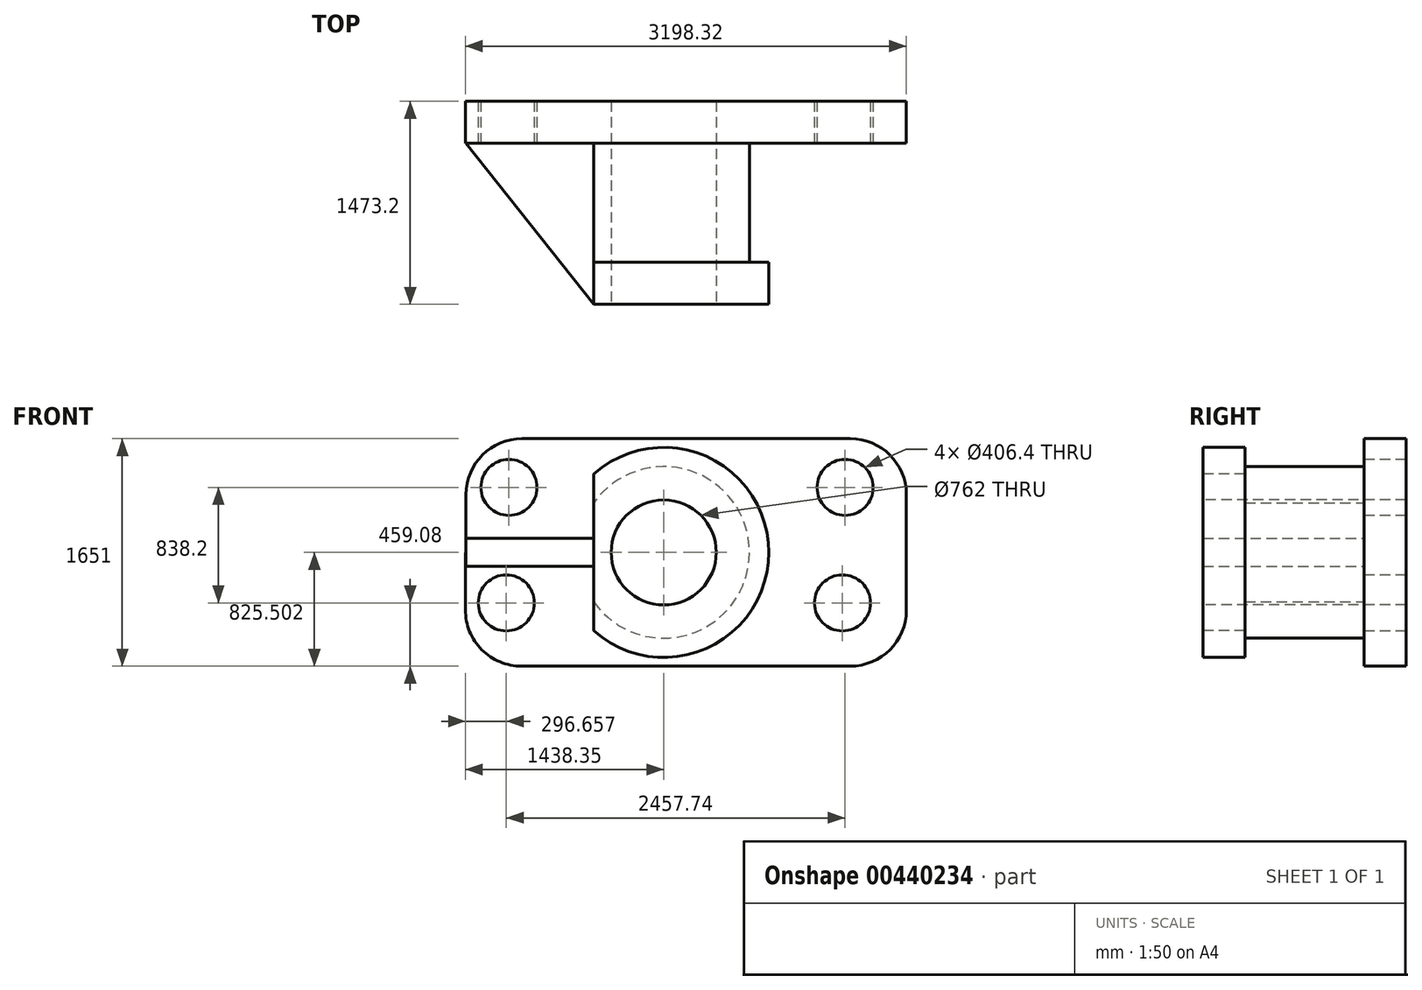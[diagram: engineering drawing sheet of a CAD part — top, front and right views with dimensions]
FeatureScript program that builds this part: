
annotation { "Feature Type Name" : "Feature", "Feature Type Description" : "" }
export const myFeature = defineFeature(function(context is Context, id is Id, definition is map)
    precondition{}
    {
        {
            var Q0;
            Q0=qCreatedBy(makeId("Front.planeOp"),FACE);
            var sketch = newSketch(context, id + "F0", { "sketchPlane" : qUnion([Q0])});
            skLineSegment(sketch, "E0", {"start": v(-1594.17, 978.7) * mm, "end": v(1597.8, 978.7) * mm});
            skLineSegment(sketch, "E1", {"start": v(1597.8, 978.7) * mm, "end": v(1597.8, -672.3) * mm});
            skLineSegment(sketch, "E2", {"start": v(1597.8, -672.3) * mm, "end": v(-1602.6, -672.3) * mm});
            skLineSegment(sketch, "E3", {"start": v(-1594.17, 978.7) * mm, "end": v(-1602.6, -672.3) * mm});
            skSolve(sketch);
        }
        {
            var Q0;
            Q0=makeQuery(id+"F0.imprint","IMPRINT",FACE,{"disambiguationData":[TD([[makeQuery(id+"F0.imprint","IMPRINT",EDGE,{"derivedFrom":sQuery(id+"F0.wireOp",EDGE,"E0")}),-1.0]])]});
            extrude(context, id + "F1", {"entities" : qUnion([Q0]), "depth" : 304.8 * mm});
        }
        {
            var Q0;
            Q0=makeQuery(id+"F1.opExtrude","CAP_FACE",FACE,{"disambiguationData":[OSD([sQuery(id+"F0.wireOp",EDGE,"E0"),sQuery(id+"F0.wireOp",EDGE,"E1"),sQuery(id+"F0.wireOp",EDGE,"E2"),sQuery(id+"F0.wireOp",EDGE,"E3")])],"isStart":false});
            var sketch = newSketch(context, id + "F2", { "sketchPlane" : qUnion([Q0])});
            skCircle(sketch, "E4", {"center": v(-1284.52, 624.97) * mm, "radius": 203.2 * mm});
            skCircle(sketch, "E5", {"center": v(-1303.86, -213.23) * mm, "radius": 203.2 * mm});
            skCircle(sketch, "E6", {"center": v(1153.88, 624.97) * mm, "radius": 203.2 * mm});
            skCircle(sketch, "E7", {"center": v(1134.54, -213.23) * mm, "radius": 203.2 * mm});
            skSolve(sketch);
        }
        {
            var Q0;
            Q0=makeQuery(id+"F2.imprint","IMPRINT",FACE,{"disambiguationData":[TD([[makeQuery(id+"F2.imprint","IMPRINT",EDGE,{"derivedFrom":sQuery(id+"F2.wireOp",EDGE,"E4")}),1.0]])]});
            var Q1;
            Q1=makeQuery(id+"F2.imprint","IMPRINT",FACE,{"disambiguationData":[TD([[makeQuery(id+"F2.imprint","IMPRINT",EDGE,{"derivedFrom":sQuery(id+"F2.wireOp",EDGE,"E5")}),1.0]])]});
            var Q2;
            Q2=makeQuery(id+"F2.imprint","IMPRINT",FACE,{"disambiguationData":[TD([[makeQuery(id+"F2.imprint","IMPRINT",EDGE,{"derivedFrom":sQuery(id+"F2.wireOp",EDGE,"E7")}),1.0]])]});
            var Q3;
            Q3=makeQuery(id+"F2.imprint","IMPRINT",FACE,{"disambiguationData":[TD([[makeQuery(id+"F2.imprint","IMPRINT",EDGE,{"derivedFrom":sQuery(id+"F2.wireOp",EDGE,"E6")}),1.0]])]});
            extrude(context, id + "F3", {"entities" : qUnion([Q0, Q1, Q2, Q3]), "operationType" : NewBodyOperationType.REMOVE, "endBound" : BoundingType.THROUGH_ALL, "oppositeDirection" : true, "depth" : 25.4 * mm});
        }
        {
            var Q0;
            Q0=makeQuery(id+"F1.opExtrude","CAP_FACE",FACE,{"disambiguationData":[OSD([sQuery(id+"F0.wireOp",EDGE,"E0"),sQuery(id+"F0.wireOp",EDGE,"E1"),sQuery(id+"F0.wireOp",EDGE,"E2"),sQuery(id+"F0.wireOp",EDGE,"E3")])],"isStart":false});
            var sketch = newSketch(context, id + "F4", { "sketchPlane" : qUnion([Q0])});
            skCircle(sketch, "E8", {"center": v(-162.17, 153.2) * mm, "radius": 622.3 * mm});
            skSolve(sketch);
        }
        {
            var Q0;
            Q0=makeQuery(id+"F4.imprint","IMPRINT",FACE,{"disambiguationData":[TD([[makeQuery(id+"F4.imprint","IMPRINT",EDGE,{"derivedFrom":sQuery(id+"F4.wireOp",EDGE,"E8")}),1.0]])]});
            extrude(context, id + "F5", {"entities" : qUnion([Q0]), "operationType" : NewBodyOperationType.ADD, "depth" : 863.6 * mm});
        }
        {
            var Q0;
            Q0=makeQuery(id+"F5.opExtrude","CAP_FACE",FACE,{"disambiguationData":[OSD([sQuery(id+"F4.wireOp",EDGE,"E8")])],"isStart":false});
            var sketch = newSketch(context, id + "F6", { "sketchPlane" : qUnion([Q0])});
            skCircle(sketch, "E9", {"center": v(-162.17, 153.2) * mm, "radius": 762 * mm});
            skSolve(sketch);
        }
        {
            var Q0;
            Q0=makeQuery(id+"F6.imprint","IMPRINT",FACE,{"disambiguationData":[TD([[makeQuery(id+"F6.imprint","IMPRINT",EDGE,{"derivedFrom":sQuery(id+"F6.wireOp",EDGE,"E9")}),1.0]])]});
            var Q1;
            Q1=makeQuery(id+"F6.imprint","IMPRINT",FACE,{"disambiguationData":[TD([[makeQuery(id+"F6.imprint","IMPRINT",EDGE,{"derivedFrom":makeQuery(id+"F5.opExtrude","CAP_EDGE",EDGE,{"disambiguationData":[OSD([sQuery(id+"F4.wireOp",EDGE,"E8")])],"isStart":false})}),1.0]])]});
            extrude(context, id + "F7", {"entities" : qUnion([Q0, Q1]), "operationType" : NewBodyOperationType.ADD, "depth" : 304.8 * mm});
        }
        {
            var Q0;
            Q0=makeQuery(id+"F7.opExtrude","CAP_FACE",FACE,{"disambiguationData":[OSD([sQuery(id+"F6.wireOp",EDGE,"E9")])],"isStart":false});
            var sketch = newSketch(context, id + "F8", { "sketchPlane" : qUnion([Q0])});
            skCircle(sketch, "E10", {"center": v(-162.17, 153.2) * mm, "radius": 381 * mm});
            skSolve(sketch);
        }
        {
            var Q0;
            Q0=makeQuery(id+"F8.imprint","IMPRINT",FACE,{"disambiguationData":[TD([[makeQuery(id+"F8.imprint","IMPRINT",EDGE,{"derivedFrom":sQuery(id+"F8.wireOp",EDGE,"E10")}),1.0]])]});
            extrude(context, id + "F9", {"entities" : qUnion([Q0]), "operationType" : NewBodyOperationType.REMOVE, "endBound" : BoundingType.THROUGH_ALL, "oppositeDirection" : true, "depth" : 25.4 * mm});
        }
        {
            var Q0;
            Q0=makeQuery(id+"F7.opExtrude","CAP_FACE",FACE,{"disambiguationData":[OSD([sQuery(id+"F6.wireOp",EDGE,"E9")])],"isStart":false});
            var sketch = newSketch(context, id + "F10", { "sketchPlane" : qUnion([Q0])});
            skCircle(sketch, "E11.0.0", {"center": v(-162.17, 153.2) * mm, "radius": 762 * mm});
            skLineSegment(sketch, "E12", {"start": v(-162.17, 915.2) * mm, "end": v(-162.17, -608.8) * mm, "construction": true});
            skLineSegment(sketch, "E13.0", {"start": v(-670.17, 721.15) * mm, "end": v(-670.17, -414.77) * mm});
            skSolve(sketch);
        }
        {
            var Q0;
            {var subQ0=sQuery(id+"F10.wireOp",EDGE,"E13.0");Q0=makeQuery(id+"F10.imprint","IMPRINT",FACE,{"disambiguationData":[TD([[makeQuery(id+"F10.imprint","IMPRINT",EDGE,{"derivedFrom":subQ0}),-1.0]])]});}
            var Q1;
            Q1=makeQuery(id+"F1.opExtrude","CAP_FACE",FACE,{"disambiguationData":[OSD([sQuery(id+"F0.wireOp",EDGE,"E0"),sQuery(id+"F0.wireOp",EDGE,"E1"),sQuery(id+"F0.wireOp",EDGE,"E2"),sQuery(id+"F0.wireOp",EDGE,"E3")])],"isStart":false});
            extrude(context, id + "F11", {"entities" : qUnion([Q0]), "operationType" : NewBodyOperationType.REMOVE, "endBound" : BoundingType.UP_TO_SURFACE, "oppositeDirection" : true, "endBoundEntityFace" : qUnion([Q1]), "depth" : 25.4 * mm});
        }
        {
            var Q0;
            Q0=makeQuery(id+"F11.boolean.opBoolean","COPY",FACE,{"derivedFrom":makeQuery(id+"F11.opExtrude","SWEPT_FACE",FACE,{"disambiguationData":[OSD([sQuery(id+"F10.wireOp",EDGE,"E13.0")])]})});
            var sketch = newSketch(context, id + "F12", { "sketchPlane" : qUnion([Q0])});
            skLineSegment(sketch, "E14", {"start": v(1473.2, 254.8) * mm, "end": v(304.8, 254.8) * mm});
            skLineSegment(sketch, "E15", {"start": v(1473.2, 51.6) * mm, "end": v(304.8, 51.6) * mm});
            skSolve(sketch);
        }
        {
            var Q0;
            {var subQ0=sQuery(id+"F12.wireOp",EDGE,"E14");Q0=makeQuery(id+"F12.imprint","IMPRINT",FACE,{"disambiguationData":[TD([[makeQuery(id+"F12.imprint","IMPRINT",EDGE,{"derivedFrom":subQ0}),1.0]])]});}
            extrude(context, id + "F13", {"entities" : qUnion([Q0]), "operationType" : NewBodyOperationType.ADD, "depth" : 927.6 * mm});
        }
        {
            var Q0;
            Q0=makeQuery(id+"F13.opExtrude","SWEPT_FACE",FACE,{"disambiguationData":[OSD([sQuery(id+"F12.wireOp",EDGE,"E14")])]});
            var sketch = newSketch(context, id + "F14", { "sketchPlane" : qUnion([Q0])});
            skLineSegment(sketch, "E16", {"start": v(-670.17, -1473.2) * mm, "end": v(-1597.78, -304.8) * mm});
            skSolve(sketch);
        }
        {
            var Q0;
            Q0=makeQuery(id+"F14.imprint","IMPRINT",FACE,{"disambiguationData":[TD([[makeQuery(id+"F14.imprint","IMPRINT",EDGE,{"derivedFrom":sQuery(id+"F14.wireOp",EDGE,"E16")}),1.0]])]});
            extrude(context, id + "F15", {"entities" : qUnion([Q0]), "operationType" : NewBodyOperationType.REMOVE, "endBound" : BoundingType.UP_TO_NEXT, "oppositeDirection" : true, "depth" : 25.4 * mm});
        }
        {
            var Q0;
            {var subQ0=sQuery(id+"F0.wireOp",EDGE,"E3");var subQ1=sQuery(id+"F0.wireOp",EDGE,"E2");var subQ2=sQuery(id+"F0.wireOp",EDGE,"E1");var subQ3=sQuery(id+"F0.wireOp",EDGE,"E0");Q0=makeQuery(id+"F11.boolean.opBoolean","MERGE",FACE,{"derivedFrom":[makeQuery(id+"F1.opExtrude","CAP_FACE",FACE,{"disambiguationData":[OSD([subQ3,subQ2,subQ1,subQ0])],"isStart":false}),makeQuery(id+"F11.opExtrude","CAP_FACE",FACE,{"disambiguationData":[OSD([subQ3,subQ2,subQ1,subQ0])],"isStart":false})]});}
            var sketch = newSketch(context, id + "F16", { "sketchPlane" : qUnion([Q0])});
            skLineSegment(sketch, "E17", {"start": v(1191.4, -672.3) * mm, "end": v(-1194.12, -672.3) * mm});
            skLineSegment(sketch, "E18", {"start": v(-1600.51, -263.84) * mm, "end": v(-1596.24, 574.36) * mm});
            skLineSegment(sketch, "E19", {"start": v(-1189.84, 978.7) * mm, "end": v(1191.4, 978.7) * mm});
            skLineSegment(sketch, "E20", {"start": v(1597.8, 572.3) * mm, "end": v(1597.8, -265.9) * mm});
            skPoint(sketch, "E21.visualSharp", {"position": v(-1602.6, -672.3) * mm});
            skArc(sketch, "E21.filletArc", {"start": v(-1600.51, -263.84) * mm, "mid": v(-1482.22, -552.54) * mm, "end": v(-1194.12, -672.3) * mm});
            skPoint(sketch, "E22.visualSharp", {"position": v(-1594.17, 978.7) * mm});
            skArc(sketch, "E22.filletArc", {"start": v(-1189.84, 978.7) * mm, "mid": v(-1476.48, 860.4) * mm, "end": v(-1596.24, 574.36) * mm});
            skPoint(sketch, "E23.visualSharp", {"position": v(1597.8, 978.7) * mm});
            skArc(sketch, "E23.filletArc", {"start": v(1597.8, 572.3) * mm, "mid": v(1478.77, 859.66) * mm, "end": v(1191.4, 978.7) * mm});
            skPoint(sketch, "E24.visualSharp", {"position": v(1597.8, -672.3) * mm});
            skArc(sketch, "E24.filletArc", {"start": v(1191.4, -672.3) * mm, "mid": v(1478.77, -553.28) * mm, "end": v(1597.8, -265.9) * mm});
            skSolve(sketch);
        }
        {
            var Q0;
            {var subQ0=sQuery(id+"F16.wireOp",EDGE,"E24.filletArc");Q0=makeQuery(id+"F16.imprint","IMPRINT",FACE,{"disambiguationData":[TD([[makeQuery(id+"F16.imprint","IMPRINT",EDGE,{"derivedFrom":subQ0}),-1.0]])]});}
            var Q1;
            {var subQ0=sQuery(id+"F16.wireOp",EDGE,"E23.filletArc");Q1=makeQuery(id+"F16.imprint","IMPRINT",FACE,{"disambiguationData":[TD([[makeQuery(id+"F16.imprint","IMPRINT",EDGE,{"derivedFrom":subQ0}),-1.0]])]});}
            var Q2;
            {var subQ0=sQuery(id+"F16.wireOp",EDGE,"E21.filletArc");Q2=makeQuery(id+"F16.imprint","IMPRINT",FACE,{"disambiguationData":[TD([[makeQuery(id+"F16.imprint","IMPRINT",EDGE,{"derivedFrom":subQ0}),-1.0]])]});}
            var Q3;
            {var subQ0=sQuery(id+"F16.wireOp",EDGE,"E22.filletArc");Q3=makeQuery(id+"F16.imprint","IMPRINT",FACE,{"disambiguationData":[TD([[makeQuery(id+"F16.imprint","IMPRINT",EDGE,{"derivedFrom":subQ0}),-1.0]])]});}
            extrude(context, id + "F17", {"entities" : qUnion([Q0, Q1, Q2, Q3]), "operationType" : NewBodyOperationType.REMOVE, "endBound" : BoundingType.THROUGH_ALL, "oppositeDirection" : true, "depth" : 25.4 * mm});
        }
    });
